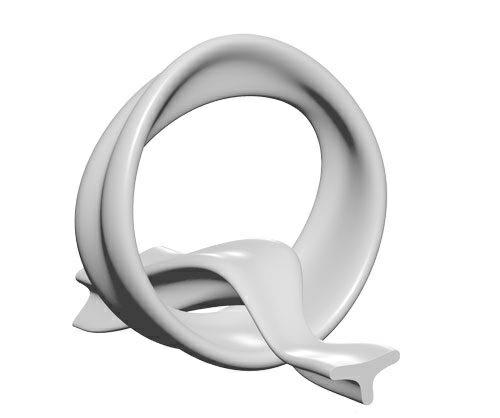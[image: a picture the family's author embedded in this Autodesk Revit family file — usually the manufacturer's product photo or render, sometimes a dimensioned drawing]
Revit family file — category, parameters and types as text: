
# Revit family: CITY ALPHABET letter „Q”
name_source: partatom
category: Furniture
revit_build: Autodesk Revit 2018 (Build: 20190510_1515(x64)
units: mm (PartAtom-declared; Revit-internal decimal feet)

## family parameters
Cut with Voids When Loaded = No
Host = Face
OmniClass Number = 23.40.10.11.14
OmniClass Title = Exterior Seating
Room Calculation Point = No
Shared = No

## types (1)
- CITY ALPHABET letter „Q"
    Default Elevation = 1219 mm
    Height = 1900 mm  [stored 6.2336 ft]
    IfcExportAs = IfcFurnishingElement
    Length = 2400 mm
    Manufacturer = Astrini Design
    Material information = Colour choice from RAL colour standard. Customer may inquire about specific request regarding individual order.
    Model = CITY ALPHABET letter „Q”
    Operating temperature = -40°C to 80°C, ( -40°F to 176°F )
    Type Comments = Bench
    Type Image = Q.jpg
    URL = https://astrini-design.pl
    Weight (approximately) = 95.00 kg
    Weight - filled (approximately) = 195.00 kg
    Width = 1850 mm  [stored 6.06955 ft]

note: [stored X ft] marks values corroborated as IEEE doubles in the binary element streams (Revit-internal decimal feet)
